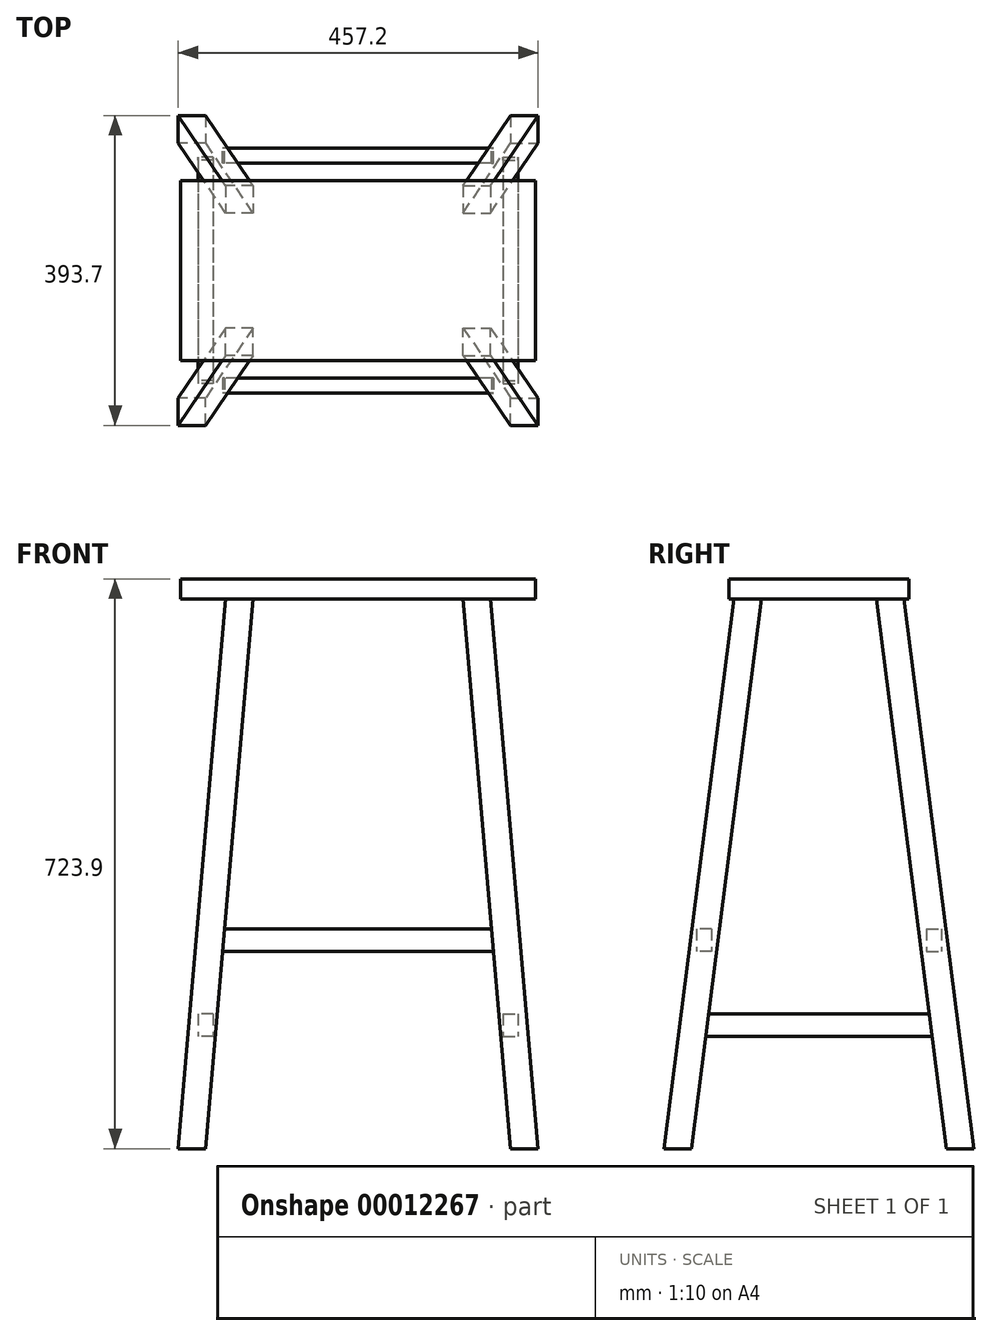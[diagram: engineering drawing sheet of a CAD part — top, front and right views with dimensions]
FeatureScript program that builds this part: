
annotation { "Feature Type Name" : "Feature", "Feature Type Description" : "" }
export const myFeature = defineFeature(function(context is Context, id is Id, definition is map)
    precondition{}
    {
        {
            var Q0;
            Q0=qCreatedBy(makeId("Top.planeOp"),FACE);
            cPlane(context, id + "F0", {"entities" : qUnion([Q0]), "cplaneType" : CPlaneType.OFFSET, "offset" : 698.5 * mm, "width" : 152.4 * mm, "height" : 152.4 * mm});
        }
        {
            var Q0;
            Q0=qCreatedBy(id+"F0.planeOp",FACE);
            var sketch = newSketch(context, id + "F1", { "sketchPlane" : qUnion([Q0])});
            skLineSegment(sketch, "E0.bottom", {"start": v(0, 0) * mm, "end": v(225.43, 0) * mm});
            skLineSegment(sketch, "E0.top", {"start": v(0, 114.3) * mm, "end": v(225.43, 114.3) * mm});
            skLineSegment(sketch, "E0.left", {"start": v(0, 0) * mm, "end": v(0, 114.3) * mm});
            skLineSegment(sketch, "E0.right", {"start": v(225.43, 0) * mm, "end": v(225.43, 114.3) * mm});
            skLineSegment(sketch, "E1.bottom", {"start": v(133.35, 107.95) * mm, "end": v(168.28, 107.95) * mm});
            skLineSegment(sketch, "E1.top", {"start": v(133.35, 73.03) * mm, "end": v(168.28, 73.03) * mm});
            skLineSegment(sketch, "E1.left", {"start": v(133.35, 107.95) * mm, "end": v(133.35, 73.03) * mm});
            skLineSegment(sketch, "E1.right", {"start": v(168.28, 107.95) * mm, "end": v(168.28, 73.03) * mm});
            skLineSegment(sketch, "E2", {"start": v(0, 323.74) * mm, "end": v(0, 0) * mm, "construction": true});
            skLineSegment(sketch, "E3", {"start": v(0, 0) * mm, "end": v(506.92, 0) * mm, "construction": true});
            skSolve(sketch);
        }
        {
            var Q0;
            Q0=qCreatedBy(makeId("Top.planeOp"),FACE);
            var sketch = newSketch(context, id + "F2", { "sketchPlane" : qUnion([Q0])});
            skLineSegment(sketch, "E4.bottom", {"start": v(193.68, 196.85) * mm, "end": v(228.6, 196.85) * mm});
            skLineSegment(sketch, "E4.top", {"start": v(193.68, 161.93) * mm, "end": v(228.6, 161.93) * mm});
            skLineSegment(sketch, "E4.left", {"start": v(193.68, 196.85) * mm, "end": v(193.68, 161.93) * mm});
            skLineSegment(sketch, "E4.right", {"start": v(228.6, 196.85) * mm, "end": v(228.6, 161.93) * mm});
            skLineSegment(sketch, "E5", {"start": v(0, 280.72) * mm, "end": v(0, 0) * mm, "construction": true});
            skLineSegment(sketch, "E6", {"start": v(0, 0) * mm, "end": v(324.6, 0) * mm, "construction": true});
            skSolve(sketch);
        }
        {
            var Q0;
            Q0=makeQuery(id+"F1.imprint","IMPRINT",FACE,{"disambiguationData":[TD([[makeQuery(id+"F1.imprint","IMPRINT",EDGE,{"derivedFrom":sQuery(id+"F1.wireOp",EDGE,"E1.bottom")}),-1.0]])]});
            var Q1;
            Q1=makeQuery(id+"F1.imprint","IMPRINT",FACE,{"disambiguationData":[TD([[makeQuery(id+"F1.imprint","IMPRINT",EDGE,{"derivedFrom":sQuery(id+"F1.wireOp",EDGE,"E0.bottom")}),1.0]])]});
            extrude(context, id + "F3", {"entities" : qUnion([Q0, Q1]), "depth" : 25.4 * mm});
        }
        {
            var Q0;
            Q0=makeQuery(id+"F1.imprint","IMPRINT",FACE,{"disambiguationData":[TD([[makeQuery(id+"F1.imprint","IMPRINT",EDGE,{"derivedFrom":sQuery(id+"F1.wireOp",EDGE,"E1.bottom")}),-1.0]])]});
            var Q1;
            Q1=makeQuery(id+"F2.imprint","IMPRINT",FACE,{"disambiguationData":[TD([[makeQuery(id+"F2.imprint","IMPRINT",EDGE,{"derivedFrom":sQuery(id+"F2.wireOp",EDGE,"E4.bottom")}),-1.0]])]});
            var Q2;
            Q2=sQuery(id+"F1.wireOp",VERTEX,"E1.right.start");
            var Q3;
            Q3=sQuery(id+"F2.wireOp",VERTEX,"E4.bottom.end");
            loft(context, id + "F4", {"operationType" : NewBodyOperationType.ADD, "sheetProfilesArray" : [{ "sheetProfileEntities" : qUnion([Q0]) }, { "sheetProfileEntities" : qUnion([Q1]) }], "matchConnections" : true, "connections" : [{ "connectionEntities" : qUnion([Q2, Q3]), "connectionEdgeQueries" : qUnion([]), "connectionEdgeParameters" : [] }]});
        }
        {
            var Q0;
            Q0=qCreatedBy(makeId("Front.planeOp"),FACE);
            var sketch = newSketch(context, id + "F5", { "sketchPlane" : qUnion([Q0])});
            skLineSegment(sketch, "E7.bottom", {"start": v(184.15, 171.45) * mm, "end": v(203.2, 171.45) * mm});
            skLineSegment(sketch, "E7.top", {"start": v(184.15, 142.88) * mm, "end": v(203.2, 142.88) * mm});
            skLineSegment(sketch, "E7.left", {"start": v(184.15, 171.45) * mm, "end": v(184.15, 142.88) * mm});
            skLineSegment(sketch, "E7.right", {"start": v(203.2, 171.45) * mm, "end": v(203.2, 142.88) * mm});
            skLineSegment(sketch, "E8", {"start": v(0, 0) * mm, "end": v(0, 345.63) * mm, "construction": true});
            skSolve(sketch);
        }
        {
            var Q0;
            Q0 = qSketchRegion(id + "F5", true);
            extrude(context, id + "F6", {"entities" : qUnion([Q0]), "operationType" : NewBodyOperationType.ADD, "endBound" : BoundingType.UP_TO_NEXT, "oppositeDirection" : true, "depth" : 25.4 * mm});
        }
        {
            var Q0;
            Q0=qCreatedBy(makeId("Right.planeOp"),FACE);
            var sketch = newSketch(context, id + "F7", { "sketchPlane" : qUnion([Q0])});
            skLineSegment(sketch, "E9.bottom", {"start": v(136.53, 279.4) * mm, "end": v(155.58, 279.4) * mm});
            skLineSegment(sketch, "E9.top", {"start": v(136.53, 250.83) * mm, "end": v(155.58, 250.83) * mm});
            skLineSegment(sketch, "E9.left", {"start": v(136.53, 279.4) * mm, "end": v(136.53, 250.83) * mm});
            skLineSegment(sketch, "E9.right", {"start": v(155.58, 279.4) * mm, "end": v(155.58, 250.83) * mm});
            skLineSegment(sketch, "E10", {"start": v(0, 0) * mm, "end": v(0, 387.54) * mm, "construction": true});
            skSolve(sketch);
        }
        {
            var Q0;
            Q0 = qSketchRegion(id + "F7", true);
            extrude(context, id + "F8", {"entities" : qUnion([Q0]), "operationType" : NewBodyOperationType.ADD, "endBound" : BoundingType.UP_TO_NEXT, "depth" : 25.4 * mm});
        }
        {
            var Q0;
            Q0=makeQuery(id+"F3.opExtrude","SWEPT_BODY",BODY,{"disambiguationData":[OSD([sQuery(id+"F1.wireOp",EDGE,"E0.bottom"),sQuery(id+"F1.wireOp",EDGE,"E0.top"),sQuery(id+"F1.wireOp",EDGE,"E0.left"),sQuery(id+"F1.wireOp",EDGE,"E0.right")])]});
            var Q1;
            Q1=qCreatedBy(makeId("Front.planeOp"),FACE);
            mirror(context, id + "F9", {"operationType" : NewBodyOperationType.ADD, "entities" : qUnion([Q0]), "mirrorPlane" : qUnion([Q1])});
        }
        {
            var Q0;
            Q0=makeQuery(id+"F3.opExtrude","SWEPT_BODY",BODY,{"disambiguationData":[OSD([sQuery(id+"F1.wireOp",EDGE,"E0.bottom"),sQuery(id+"F1.wireOp",EDGE,"E0.top"),sQuery(id+"F1.wireOp",EDGE,"E0.left"),sQuery(id+"F1.wireOp",EDGE,"E0.right")])]});
            var Q1;
            Q1=qCreatedBy(makeId("Right.planeOp"),FACE);
            mirror(context, id + "F10", {"operationType" : NewBodyOperationType.ADD, "entities" : qUnion([Q0]), "mirrorPlane" : qUnion([Q1])});
        }
    });
